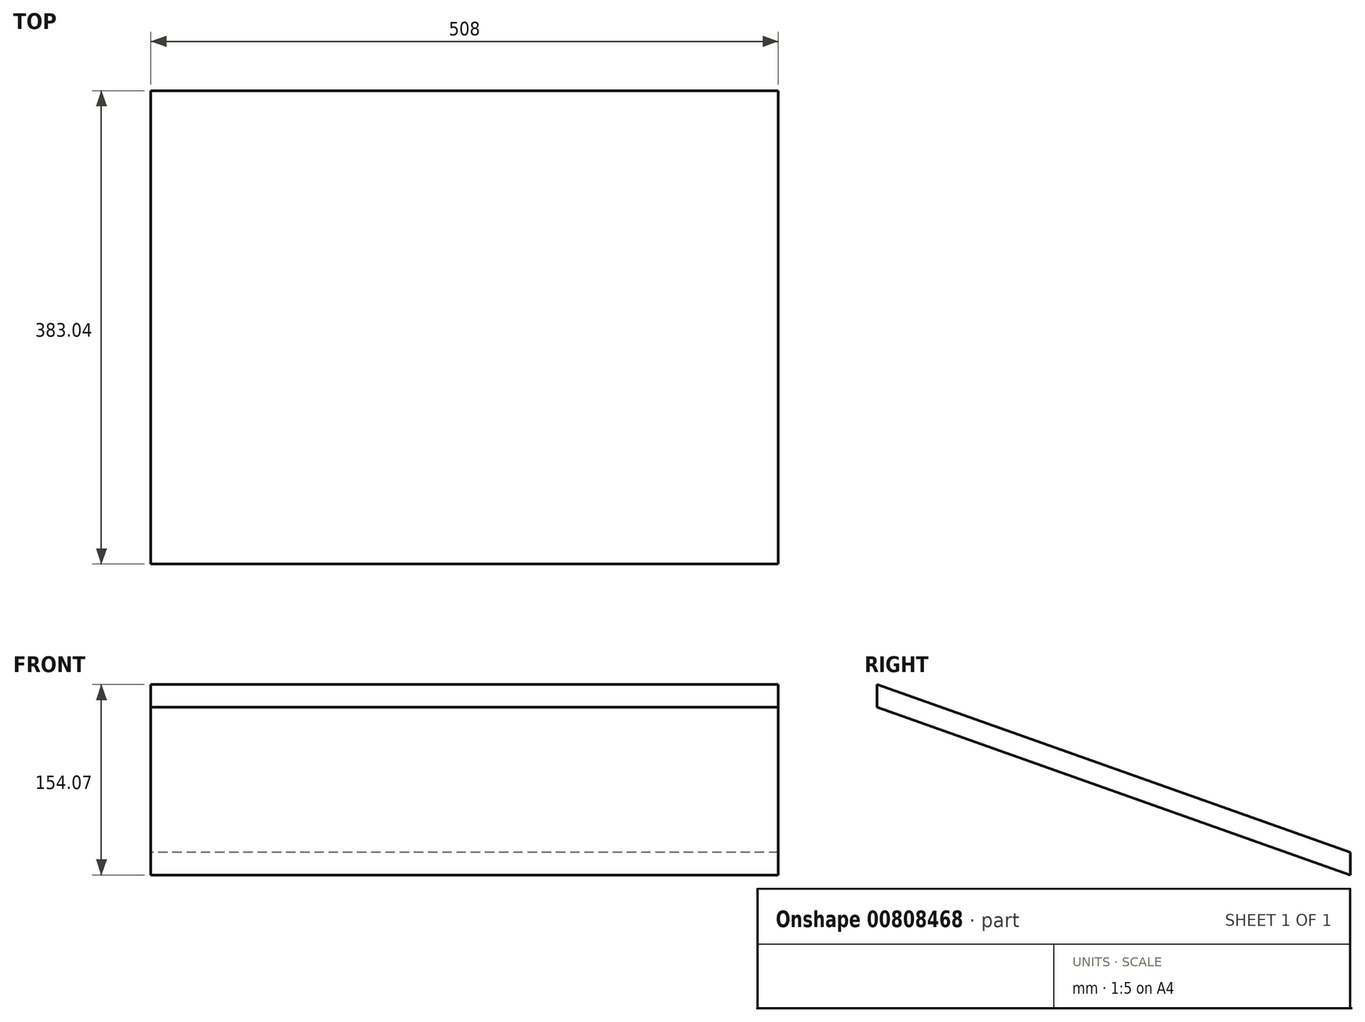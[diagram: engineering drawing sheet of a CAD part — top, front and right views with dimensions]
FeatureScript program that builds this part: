
annotation { "Feature Type Name" : "Feature", "Feature Type Description" : "" }
export const myFeature = defineFeature(function(context is Context, id is Id, definition is map)
    precondition{}
    {
        {
            var Q0;
            Q0=qCreatedBy(makeId("Right.planeOp"),FACE);
            var sketch = newSketch(context, id + "F0", { "sketchPlane" : qUnion([Q0])});
            skLineSegment(sketch, "E0", {"start": v(-152.72, -69.6) * mm, "end": v(133.82, -69.6) * mm});
            skLineSegment(sketch, "E1", {"start": v(133.82, -69.6) * mm, "end": v(-152.72, 32) * mm});
            skLineSegment(sketch, "E2", {"start": v(-152.72, 32) * mm, "end": v(-152.72, -69.6) * mm});
            skSolve(sketch);
        }
        {
            var Q0;
            Q0=qCreatedBy(makeId("Right.planeOp"),FACE);
            var sketch = newSketch(context, id + "F1", { "sketchPlane" : qUnion([Q0])});
            skLineSegment(sketch, "E3", {"start": v(-79.72, 29.34) * mm, "end": v(-79.72, 11.08) * mm});
            skLineSegment(sketch, "E4", {"start": v(-79.72, 11.08) * mm, "end": v(303.32, -124.73) * mm});
            skLineSegment(sketch, "E5", {"start": v(303.32, -124.73) * mm, "end": v(303.32, -106.47) * mm});
            skLineSegment(sketch, "E6", {"start": v(303.32, -106.47) * mm, "end": v(-79.72, 29.34) * mm});
            skSolve(sketch);
        }
        {
            var Q0;
            Q0 = qSketchRegion(id + "F1", true);
            extrude(context, id + "F2", {"entities" : qUnion([Q0]), "depth" : 508 * mm, "offsetDistance" : 25.4 * mm});
        }
    });
